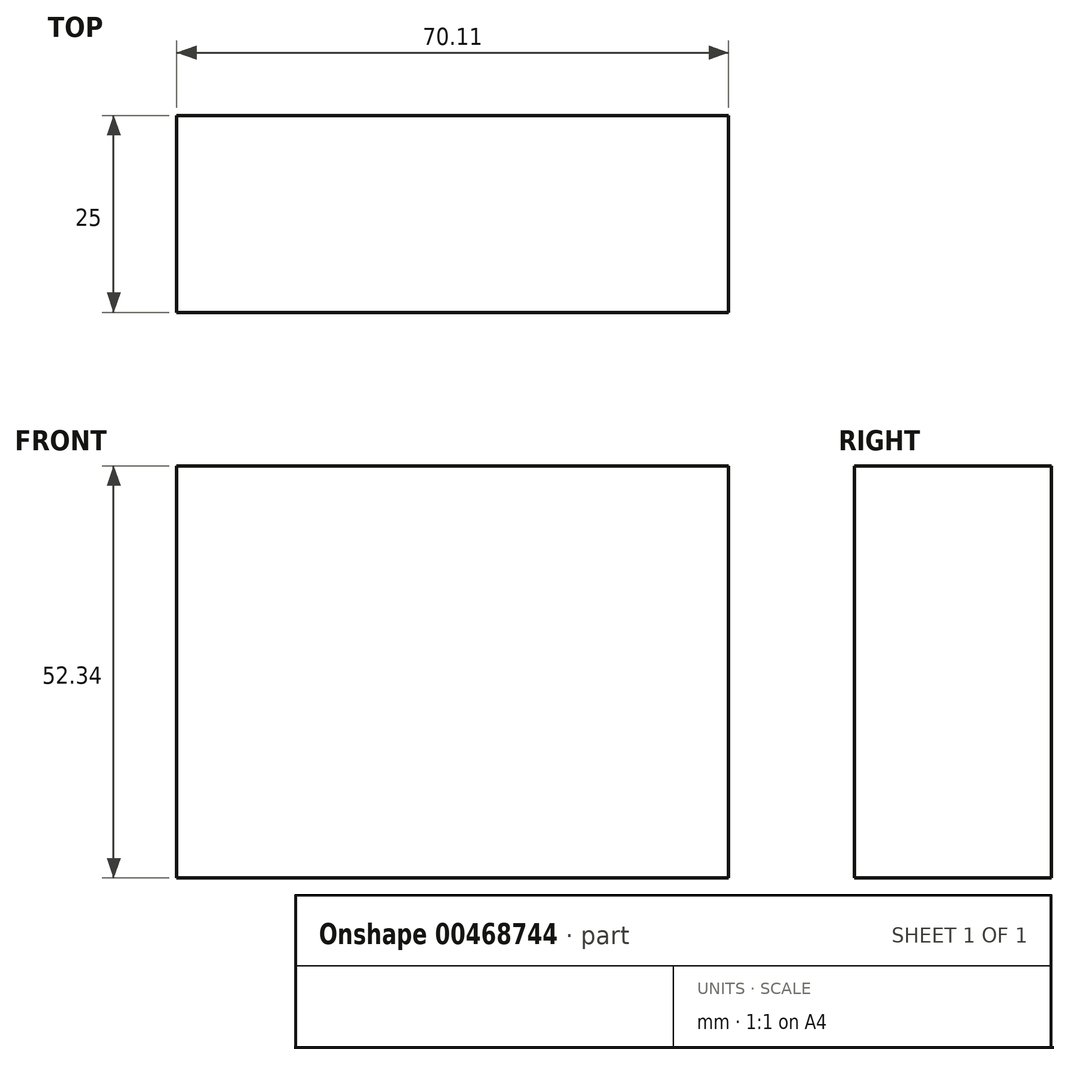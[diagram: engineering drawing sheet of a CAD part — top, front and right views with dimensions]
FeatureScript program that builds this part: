
annotation { "Feature Type Name" : "Feature", "Feature Type Description" : "" }
export const myFeature = defineFeature(function(context is Context, id is Id, definition is map)
    precondition{}
    {
        {
            var Q0;
            Q0=qCreatedBy(makeId("Front.planeOp"),FACE);
            var sketch = newSketch(context, id + "F0", { "sketchPlane" : qUnion([Q0])});
            skLineSegment(sketch, "E0.bottom", {"start": v(0, 0) * mm, "end": v(-70.11, 0) * mm});
            skLineSegment(sketch, "E0.top", {"start": v(0, 52.34) * mm, "end": v(-70.11, 52.34) * mm});
            skLineSegment(sketch, "E0.left", {"start": v(0, 0) * mm, "end": v(0, 52.34) * mm});
            skLineSegment(sketch, "E0.right", {"start": v(-70.11, 0) * mm, "end": v(-70.11, 52.34) * mm});
            skSolve(sketch);
        }
        {
            var Q0;
            Q0 = qSketchRegion(id + "F0", true);
            extrude(context, id + "F1", {"entities" : qUnion([Q0]), "depth" : 25 * mm});
        }
    });
